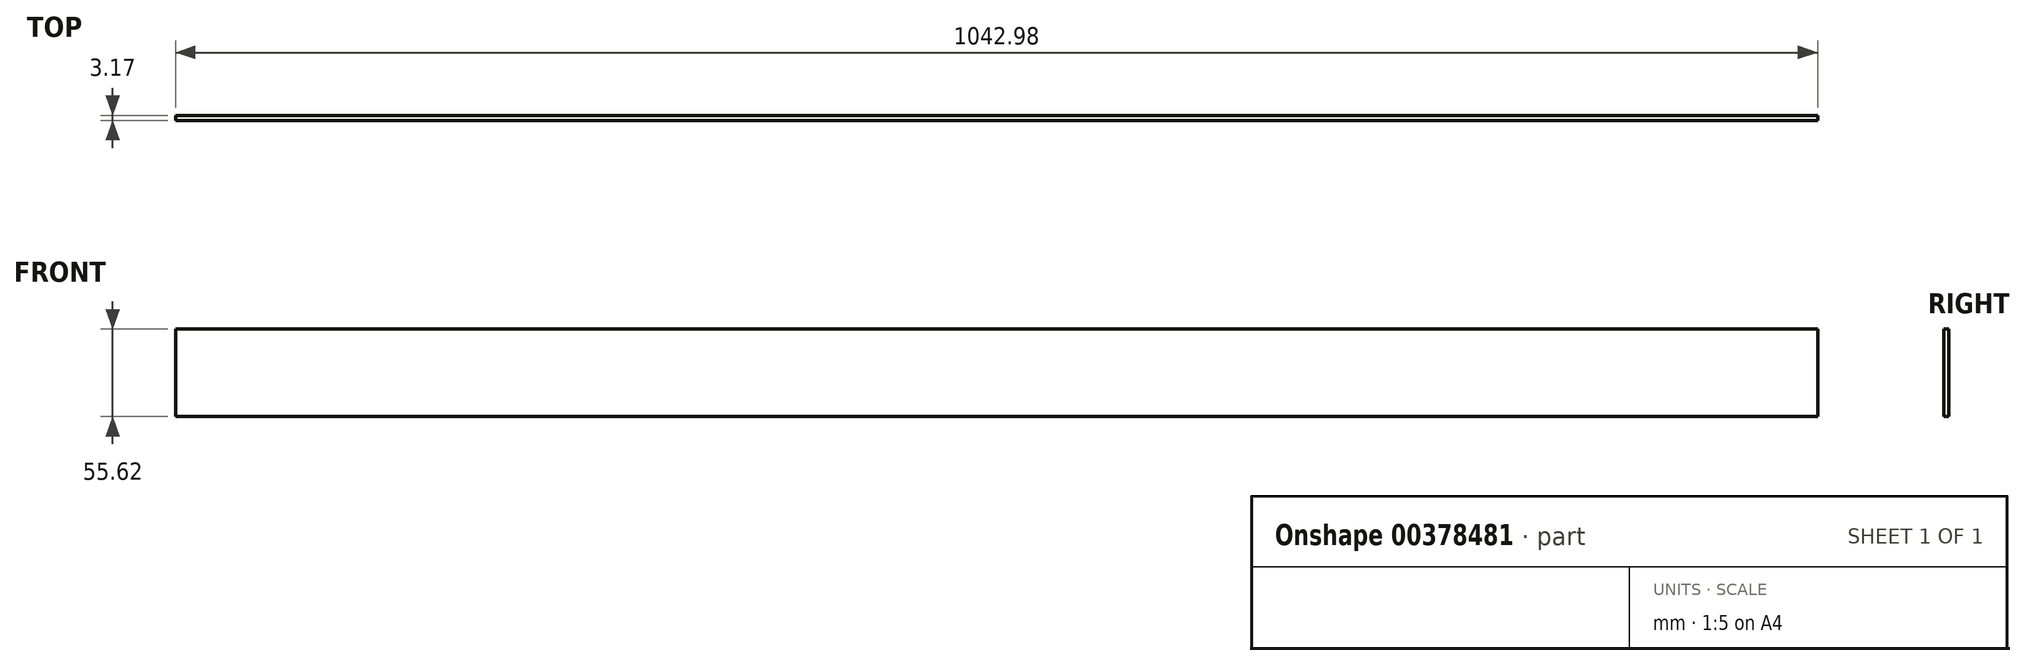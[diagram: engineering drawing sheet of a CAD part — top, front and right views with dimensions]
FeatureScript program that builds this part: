
annotation { "Feature Type Name" : "Feature", "Feature Type Description" : "" }
export const myFeature = defineFeature(function(context is Context, id is Id, definition is map)
    precondition{}
    {
        {
            var Q0;
            Q0=qCreatedBy(makeId("Front.planeOp"),FACE);
            var sketch = newSketch(context, id + "F0", { "sketchPlane" : qUnion([Q0])});
            skLineSegment(sketch, "E0.bottom", {"start": v(521.5, 27.81) * mm, "end": v(-521.5, 27.81) * mm});
            skLineSegment(sketch, "E0.top", {"start": v(521.5, -27.81) * mm, "end": v(-521.5, -27.81) * mm});
            skLineSegment(sketch, "E0.left", {"start": v(521.5, 27.81) * mm, "end": v(521.5, -27.81) * mm});
            skLineSegment(sketch, "E0.right", {"start": v(-521.5, 27.81) * mm, "end": v(-521.5, -27.81) * mm});
            skPoint(sketch, "E0.middle", {"position": v(0, 0) * mm});
            skSolve(sketch);
        }
        {
            var Q0;
            Q0 = qSketchRegion(id + "F0", true);
            extrude(context, id + "F1", {"entities" : qUnion([Q0]), "depth" : 3.17 * mm});
        }
    });
